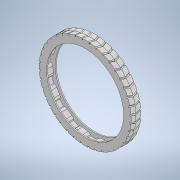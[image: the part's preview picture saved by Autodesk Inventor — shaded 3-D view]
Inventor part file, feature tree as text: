
AUTODESK INVENTOR PART (.ipt)
format: ipt  version: 2022 (Build 260153000, 153)  size: 1,184,256 bytes
history: native  units: mm
features: sketch x4, projected_geometry x4, other x3, extrude x2, plane x2, mirror x2, boolean_combine x1, loft x1, pattern_circular x1
ambient origin geometry x8: Origin, YZ Plane, XZ Plane, XY Plane, X Axis, Y Axis, Z Axis, Center Point
bodies: Solid2 (feature_tree), Solid3 (feature_tree), Solid1 (feature_tree)
feature tree (20):
  other  "Wheel.ipt"
  extrude  "Extrusion1"  Depth=10.0mm
  extrude  "Extrusion2"  Depth=1.0mm TaperAngle=0.0deg
  plane  "Work Plane1"
  mirror  "Mirror1"
  boolean_combine  "Combine1"
  sketch  "Sketch3"  dims[d5=6.65mm d6=0.0mm d8=1.0mm]
  plane  "Work Plane2"
  sketch  "Sketch4"  dims[d9=30.0deg d10=30.0deg d11=5.0mm d12=1.0mm d13=5.0mm d14=30.0deg d15=30.0deg d16=0.349066mm d17=0.0mm d18=90.0deg d19=0.0mm d20=90.0deg d21=400.0mm d22=360.0deg d24=0.2mm]
  loft  "Loft1"
  mirror  "Mirror2"
  pattern_circular  "Circular Pattern1"  Angle=30.0deg  [1 undecoded]
  other  "Solid2::Wheel.ipt"
  other  "TaggingFeature1"
  sketch  "Sketch1"  dims[d0=10.0mm d1=2.0mm]
  projected_geometry  "Projected Loop1"
  sketch  "Sketch2"  dims[d2=2.0mm d3=1.0mm d4=0.0mm]
  projected_geometry  "Projected Loop4"
  projected_geometry  "Projected Loop5"
  projected_geometry  "Projected Loop6"
note: 1 required parameter value undecoded (feature->parameter linkage not recoverable at this tier; creation-order binding heuristic only, values carry confidence <= 0.55)
